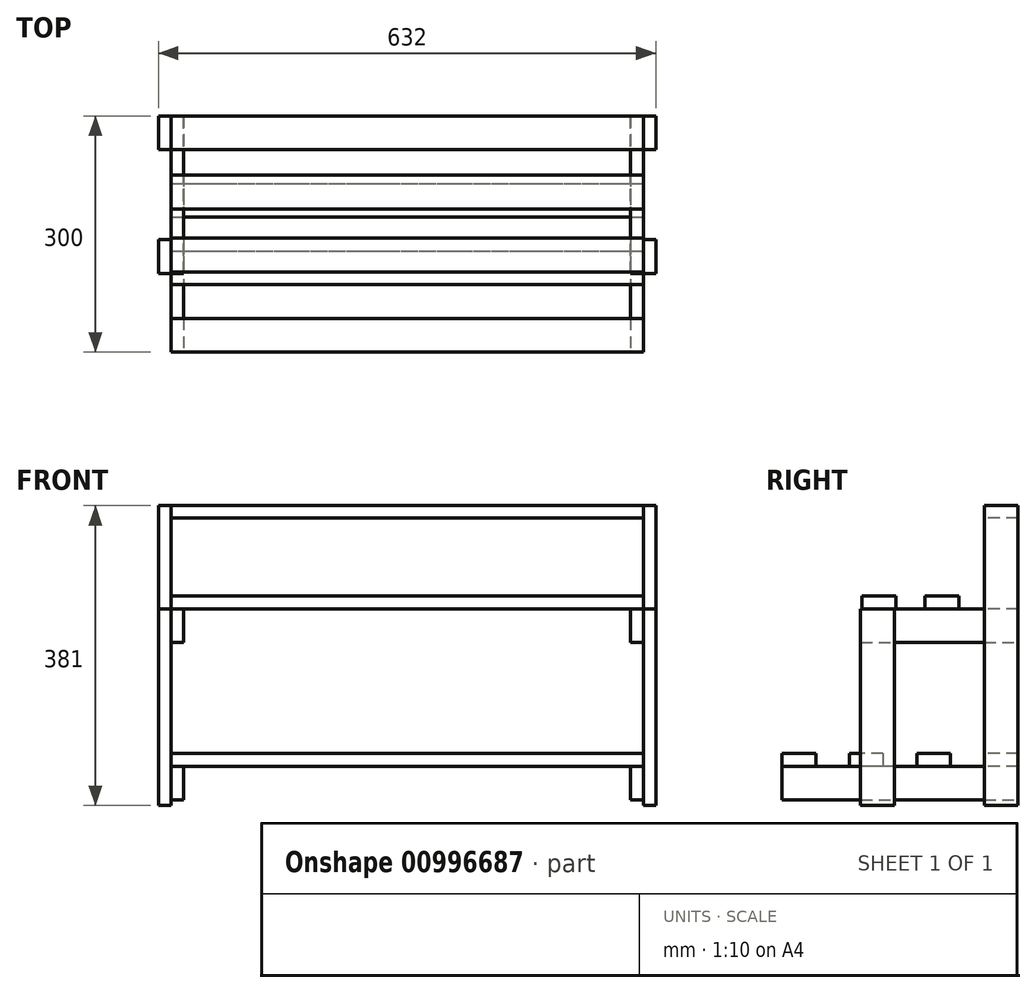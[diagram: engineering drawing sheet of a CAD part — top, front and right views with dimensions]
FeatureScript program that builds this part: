
annotation { "Feature Type Name" : "Feature", "Feature Type Description" : "" }
export const myFeature = defineFeature(function(context is Context, id is Id, definition is map)
    precondition{}
    {
        {
            var Q0;
            Q0=qCreatedBy(makeId("Top.planeOp"),FACE);
            var sketch = newSketch(context, id + "F0", { "sketchPlane" : qUnion([Q0])});
            skLineSegment(sketch, "E0.bottom", {"start": v(-351.68, 45.9) * mm, "end": v(248.32, 45.9) * mm});
            skLineSegment(sketch, "E0.top", {"start": v(-351.68, 2.9) * mm, "end": v(248.32, 2.9) * mm});
            skLineSegment(sketch, "E0.left", {"start": v(-351.68, 45.9) * mm, "end": v(-351.68, 2.9) * mm});
            skLineSegment(sketch, "E0.right", {"start": v(248.32, 45.9) * mm, "end": v(248.32, 2.9) * mm});
            skSolve(sketch);
        }
        {
            var Q0;
            Q0 = qSketchRegion(id + "F0", true);
            extrude(context, id + "F1", {"entities" : qUnion([Q0]), "depth" : 16 * mm, "offsetDistance" : 25 * mm});
        }
        {
            var Q0;
            Q0=makeQuery(id+"F1.opExtrude","SWEPT_BODY",BODY,{"disambiguationData":[OSD([sQuery(id+"F0.wireOp",EDGE,"E0.bottom"),sQuery(id+"F0.wireOp",EDGE,"E0.top"),sQuery(id+"F0.wireOp",EDGE,"E0.left"),sQuery(id+"F0.wireOp",EDGE,"E0.right")])]});
            transform(context, id + "F2", {"entities" : qUnion([Q0]), "transformType" : TransformType.TRANSLATION_3D, "dx" : 0 * mm, "dy" : -50 * mm, "dz" : -115 * mm, "makeCopy" : true});
        }
        {
            var Q0;
            Q0=makeQuery(id+"F2.opPattern","COPY",BODY,{"derivedFrom":makeQuery(id+"F1.opExtrude","SWEPT_BODY",BODY,{"disambiguationData":[OSD([sQuery(id+"F0.wireOp",EDGE,"E0.bottom"),sQuery(id+"F0.wireOp",EDGE,"E0.top"),sQuery(id+"F0.wireOp",EDGE,"E0.left"),sQuery(id+"F0.wireOp",EDGE,"E0.right")])]}),"instanceName":"1"});
            transform(context, id + "F3", {"entities" : qUnion([Q0]), "transformType" : TransformType.TRANSLATION_3D, "dx" : 0 * mm, "dy" : -95 * mm, "dz" : 0 * mm, "makeCopy" : true});
        }
        {
            var Q0;
            Q0=makeQuery(id+"F3.opPattern","COPY",BODY,{"derivedFrom":makeQuery(id+"F2.opPattern","COPY",BODY,{"derivedFrom":makeQuery(id+"F1.opExtrude","SWEPT_BODY",BODY,{"disambiguationData":[OSD([sQuery(id+"F0.wireOp",EDGE,"E0.bottom"),sQuery(id+"F0.wireOp",EDGE,"E0.top"),sQuery(id+"F0.wireOp",EDGE,"E0.left"),sQuery(id+"F0.wireOp",EDGE,"E0.right")])]}),"instanceName":"1"}),"instanceName":"1"});
            transform(context, id + "F4", {"entities" : qUnion([Q0]), "transformType" : TransformType.TRANSLATION_3D, "dx" : 0 * mm, "dy" : -155 * mm, "dz" : -200 * mm, "makeCopy" : true});
        }
        {
            var Q0;
            Q0=makeQuery(id+"F4.opPattern","COPY",BODY,{"derivedFrom":makeQuery(id+"F3.opPattern","COPY",BODY,{"derivedFrom":makeQuery(id+"F2.opPattern","COPY",BODY,{"derivedFrom":makeQuery(id+"F1.opExtrude","SWEPT_BODY",BODY,{"disambiguationData":[OSD([sQuery(id+"F0.wireOp",EDGE,"E0.bottom"),sQuery(id+"F0.wireOp",EDGE,"E0.top"),sQuery(id+"F0.wireOp",EDGE,"E0.left"),sQuery(id+"F0.wireOp",EDGE,"E0.right")])]}),"instanceName":"1"}),"instanceName":"1"}),"instanceName":"1"});
            transform(context, id + "F5", {"entities" : qUnion([Q0]), "transformType" : TransformType.TRANSLATION_3D, "dx" : 0 * mm, "dy" : 100 * mm, "dz" : 0 * mm, "makeCopy" : true});
        }
        {
            var Q0;
            Q0=makeQuery(id+"F5.opPattern","COPY",BODY,{"derivedFrom":makeQuery(id+"F4.opPattern","COPY",BODY,{"derivedFrom":makeQuery(id+"F3.opPattern","COPY",BODY,{"derivedFrom":makeQuery(id+"F2.opPattern","COPY",BODY,{"derivedFrom":makeQuery(id+"F1.opExtrude","SWEPT_BODY",BODY,{"disambiguationData":[OSD([sQuery(id+"F0.wireOp",EDGE,"E0.bottom"),sQuery(id+"F0.wireOp",EDGE,"E0.top"),sQuery(id+"F0.wireOp",EDGE,"E0.left"),sQuery(id+"F0.wireOp",EDGE,"E0.right")])]}),"instanceName":"1"}),"instanceName":"1"}),"instanceName":"1"}),"instanceName":"1"});
            transform(context, id + "F6", {"entities" : qUnion([Q0]), "transformType" : TransformType.TRANSLATION_3D, "dx" : 0 * mm, "dy" : 100 * mm, "dz" : 0 * mm, "makeCopy" : true});
        }
        {
            var Q0;
            Q0=makeQuery(id+"F6.opPattern","COPY",BODY,{"derivedFrom":makeQuery(id+"F5.opPattern","COPY",BODY,{"derivedFrom":makeQuery(id+"F4.opPattern","COPY",BODY,{"derivedFrom":makeQuery(id+"F3.opPattern","COPY",BODY,{"derivedFrom":makeQuery(id+"F2.opPattern","COPY",BODY,{"derivedFrom":makeQuery(id+"F1.opExtrude","SWEPT_BODY",BODY,{"disambiguationData":[OSD([sQuery(id+"F0.wireOp",EDGE,"E0.bottom"),sQuery(id+"F0.wireOp",EDGE,"E0.top"),sQuery(id+"F0.wireOp",EDGE,"E0.left"),sQuery(id+"F0.wireOp",EDGE,"E0.right")])]}),"instanceName":"1"}),"instanceName":"1"}),"instanceName":"1"}),"instanceName":"1"}),"instanceName":"1"});
            transform(context, id + "F7", {"entities" : qUnion([Q0]), "transformType" : TransformType.TRANSLATION_3D, "dx" : 0 * mm, "dy" : 100 * mm, "dz" : 0 * mm, "makeCopy" : true});
        }
        {
            var Q0;
            Q0=makeQuery(id+"F7.opPattern","COPY",FACE,{"derivedFrom":makeQuery(id+"F6.opPattern","COPY",FACE,{"derivedFrom":makeQuery(id+"F5.opPattern","COPY",FACE,{"derivedFrom":makeQuery(id+"F4.opPattern","COPY",FACE,{"derivedFrom":makeQuery(id+"F3.opPattern","COPY",FACE,{"derivedFrom":makeQuery(id+"F2.opPattern","COPY",FACE,{"derivedFrom":makeQuery(id+"F1.opExtrude","CAP_FACE",FACE,{"disambiguationData":[OSD([sQuery(id+"F0.wireOp",EDGE,"E0.bottom"),sQuery(id+"F0.wireOp",EDGE,"E0.top"),sQuery(id+"F0.wireOp",EDGE,"E0.left"),sQuery(id+"F0.wireOp",EDGE,"E0.right")])],"isStart":true}),"instanceName":"1"}),"instanceName":"1"}),"instanceName":"1"}),"instanceName":"1"}),"instanceName":"1"}),"instanceName":"1"});
            var sketch = newSketch(context, id + "F8", { "sketchPlane" : qUnion([Q0])});
            skLineSegment(sketch, "E1.bottom", {"start": v(-351.68, -45.9) * mm, "end": v(-351.68, -45.9) * mm});
            skLineSegment(sketch, "E1.top", {"start": v(-351.68, -2.9) * mm, "end": v(-351.68, -2.9) * mm});
            skLineSegment(sketch, "E1.left", {"start": v(-351.68, -45.9) * mm, "end": v(-351.68, -2.9) * mm});
            skLineSegment(sketch, "E1.right", {"start": v(-351.68, -45.9) * mm, "end": v(-351.68, -2.9) * mm});
            skLineSegment(sketch, "E2.bottom", {"start": v(-367.68, -2.9) * mm, "end": v(-351.68, -2.9) * mm});
            skLineSegment(sketch, "E2.top", {"start": v(-367.68, -45.9) * mm, "end": v(-351.68, -45.9) * mm});
            skLineSegment(sketch, "E2.left", {"start": v(-367.68, -2.9) * mm, "end": v(-367.68, -45.9) * mm});
            skLineSegment(sketch, "E2.right", {"start": v(-351.68, -2.9) * mm, "end": v(-351.68, -45.9) * mm});
            skSolve(sketch);
        }
        {
            var Q0;
            Q0=makeQuery(id+"F8.imprint","IMPRINT",FACE,{"disambiguationData":[TD([[makeQuery(id+"F8.imprint","IMPRINT",EDGE,{"derivedFrom":sQuery(id+"F8.wireOp",EDGE,"E2.bottom")}),-1.0]])]});
            var Q1;
            Q1=makeQuery(id+"F1.opExtrude","CAP_FACE",FACE,{"disambiguationData":[OSD([sQuery(id+"F0.wireOp",EDGE,"E0.bottom"),sQuery(id+"F0.wireOp",EDGE,"E0.top"),sQuery(id+"F0.wireOp",EDGE,"E0.left"),sQuery(id+"F0.wireOp",EDGE,"E0.right")])],"isStart":false});
            extrude(context, id + "F9", {"entities" : qUnion([Q0]), "endBound" : BoundingType.UP_TO_SURFACE, "oppositeDirection" : true, "depth" : 25 * mm, "endBoundEntityFace" : qUnion([Q1]), "offsetDistance" : 25 * mm, "hasSecondDirection" : true, "secondDirectionOppositeDirection" : false, "secondDirectionDepth" : 50 * mm});
        }
        {
            var Q0;
            Q0=makeQuery(id+"F9.opExtrude","SWEPT_BODY",BODY,{"disambiguationData":[OSD([sQuery(id+"F8.wireOp",EDGE,"E2.bottom"),sQuery(id+"F8.wireOp",EDGE,"E2.top"),sQuery(id+"F8.wireOp",EDGE,"E2.left"),sQuery(id+"F8.wireOp",EDGE,"E2.right")])]});
            var Q1;
            Q1=makeQuery(id+"F7.opPattern","COPY",EDGE,{"derivedFrom":makeQuery(id+"F6.opPattern","COPY",EDGE,{"derivedFrom":makeQuery(id+"F5.opPattern","COPY",EDGE,{"derivedFrom":makeQuery(id+"F4.opPattern","COPY",EDGE,{"derivedFrom":makeQuery(id+"F3.opPattern","COPY",EDGE,{"derivedFrom":makeQuery(id+"F2.opPattern","COPY",EDGE,{"derivedFrom":makeQuery(id+"F1.opExtrude","CAP_EDGE",EDGE,{"disambiguationData":[OSD([sQuery(id+"F0.wireOp",EDGE,"E0.bottom")])],"isStart":true}),"instanceName":"1"}),"instanceName":"1"}),"instanceName":"1"}),"instanceName":"1"}),"instanceName":"1"}),"instanceName":"1"});
            var Q2;
            Q2=makeQuery(id+"F7.opPattern","COPY",EDGE,{"derivedFrom":makeQuery(id+"F6.opPattern","COPY",EDGE,{"derivedFrom":makeQuery(id+"F5.opPattern","COPY",EDGE,{"derivedFrom":makeQuery(id+"F4.opPattern","COPY",EDGE,{"derivedFrom":makeQuery(id+"F3.opPattern","COPY",EDGE,{"derivedFrom":makeQuery(id+"F2.opPattern","COPY",EDGE,{"derivedFrom":makeQuery(id+"F1.opExtrude","CAP_EDGE",EDGE,{"disambiguationData":[OSD([sQuery(id+"F0.wireOp",EDGE,"E0.bottom")])],"isStart":true}),"instanceName":"1"}),"instanceName":"1"}),"instanceName":"1"}),"instanceName":"1"}),"instanceName":"1"}),"instanceName":"1"});
            transform(context, id + "F10", {"entities" : qUnion([Q0]), "transformType" : TransformType.TRANSLATION_DISTANCE, "transformDirection" : qUnion([Q2]), "distance" : 616 * mm, "makeCopy" : true});
        }
        {
            var Q0;
            Q0=makeQuery(id+"F2.opPattern","COPY",FACE,{"derivedFrom":makeQuery(id+"F1.opExtrude","SWEPT_FACE",FACE,{"disambiguationData":[OSD([sQuery(id+"F0.wireOp",EDGE,"E0.left")])]}),"instanceName":"1"});
            var sketch = newSketch(context, id + "F11", { "sketchPlane" : qUnion([Q0])});
            skLineSegment(sketch, "E3", {"start": v(-45.9, -115) * mm, "end": v(202.8, -115) * mm});
            skLineSegment(sketch, "E4", {"start": v(202.8, -115) * mm, "end": v(202.8, -158) * mm});
            skLineSegment(sketch, "E5", {"start": v(202.8, -158) * mm, "end": v(-45.9, -158) * mm});
            skLineSegment(sketch, "E6", {"start": v(-45.9, -158) * mm, "end": v(-45.9, -115) * mm});
            skSolve(sketch);
        }
        {
            var Q0;
            Q0 = qSketchRegion(id + "F11", true);
            extrude(context, id + "F12", {"entities" : qUnion([Q0]), "oppositeDirection" : true, "depth" : 16 * mm, "offsetDistance" : 25 * mm});
        }
        {
            var Q0;
            Q0=makeQuery(id+"F12.opExtrude","SWEPT_BODY",BODY,{"disambiguationData":[OSD([sQuery(id+"F11.wireOp",EDGE,"E3"),sQuery(id+"F11.wireOp",EDGE,"E4"),sQuery(id+"F11.wireOp",EDGE,"E5"),sQuery(id+"F11.wireOp",EDGE,"E6")])]});
            var Q1;
            Q1=makeQuery(id+"F2.opPattern","COPY",EDGE,{"derivedFrom":makeQuery(id+"F1.opExtrude","CAP_EDGE",EDGE,{"disambiguationData":[OSD([sQuery(id+"F0.wireOp",EDGE,"E0.bottom")])],"isStart":true}),"instanceName":"1"});
            transform(context, id + "F13", {"entities" : qUnion([Q0]), "transformType" : TransformType.TRANSLATION_DISTANCE, "transformDirection" : qUnion([Q1]), "distance" : (600 - 16) * mm, "makeCopy" : true});
        }
        {
            var Q0;
            Q0=makeQuery(id+"F2.opPattern","COPY",BODY,{"derivedFrom":makeQuery(id+"F1.opExtrude","SWEPT_BODY",BODY,{"disambiguationData":[OSD([sQuery(id+"F0.wireOp",EDGE,"E0.bottom"),sQuery(id+"F0.wireOp",EDGE,"E0.top"),sQuery(id+"F0.wireOp",EDGE,"E0.left"),sQuery(id+"F0.wireOp",EDGE,"E0.right")])]}),"instanceName":"1"});
            var Q1;
            Q1=makeQuery(id+"F12.opExtrude","CAP_EDGE",EDGE,{"disambiguationData":[OSD([sQuery(id+"F11.wireOp",EDGE,"E3")])],"isStart":false});
            transform(context, id + "F14", {"entities" : qUnion([Q0]), "transformType" : TransformType.TRANSLATION_DISTANCE, "transformDirection" : qUnion([Q1]), "distance" : 25 * mm, "makeCopy" : false});
        }
        {
            var Q0;
            Q0=makeQuery(id+"F3.opPattern","COPY",BODY,{"derivedFrom":makeQuery(id+"F2.opPattern","COPY",BODY,{"derivedFrom":makeQuery(id+"F1.opExtrude","SWEPT_BODY",BODY,{"disambiguationData":[OSD([sQuery(id+"F0.wireOp",EDGE,"E0.bottom"),sQuery(id+"F0.wireOp",EDGE,"E0.top"),sQuery(id+"F0.wireOp",EDGE,"E0.left"),sQuery(id+"F0.wireOp",EDGE,"E0.right")])]}),"instanceName":"1"}),"instanceName":"1"});
            var Q1;
            Q1=makeQuery(id+"F12.opExtrude","CAP_EDGE",EDGE,{"disambiguationData":[OSD([sQuery(id+"F11.wireOp",EDGE,"E3")])],"isStart":false});
            transform(context, id + "F15", {"entities" : qUnion([Q0]), "transformType" : TransformType.TRANSLATION_DISTANCE, "transformDirection" : qUnion([Q1]), "distance" : 25 * mm, "makeCopy" : false});
        }
        {
            var Q0;
            Q0=makeQuery(id+"F12.opExtrude","SWEPT_BODY",BODY,{"disambiguationData":[OSD([sQuery(id+"F11.wireOp",EDGE,"E3"),sQuery(id+"F11.wireOp",EDGE,"E4"),sQuery(id+"F11.wireOp",EDGE,"E5"),sQuery(id+"F11.wireOp",EDGE,"E6")])]});
            var Q1;
            Q1=makeQuery(id+"F9.opExtrude","SWEPT_EDGE",EDGE,{"disambiguationData":[OSD([sQuery(id+"F0.wireOp",EDGE,"E0.bottom"),sQuery(id+"F8.wireOp",EDGE,"E2.top"),sQuery(id+"F8.wireOp",EDGE,"E2.right")])]});
            transform(context, id + "F16", {"entities" : qUnion([Q0]), "transformType" : TransformType.TRANSLATION_DISTANCE, "transformDirection" : qUnion([Q1]), "distance" : 200 * mm, "makeCopy" : true});
        }
        {
            var Q0;
            Q0=makeQuery(id+"F16.opPattern","COPY",FACE,{"derivedFrom":makeQuery(id+"F12.opExtrude","SWEPT_FACE",FACE,{"disambiguationData":[OSD([sQuery(id+"F11.wireOp",EDGE,"E4")])]}),"instanceName":"1"});
            extrude(context, id + "F17", {"entities" : qUnion([Q0]), "operationType" : NewBodyOperationType.ADD, "depth" : 51.3 * mm, "offsetDistance" : 25 * mm});
        }
        {
            var Q0;
            Q0=makeQuery(id+"F12.opExtrude","SWEPT_FACE",FACE,{"disambiguationData":[OSD([sQuery(id+"F11.wireOp",EDGE,"E4")])]});
            extrude(context, id + "F18", {"entities" : qUnion([Q0]), "operationType" : NewBodyOperationType.REMOVE, "oppositeDirection" : true, "depth" : 48.7 * mm, "offsetDistance" : 25 * mm});
        }
        {
            var Q0;
            Q0=makeQuery(id+"F13.opPattern","COPY",FACE,{"derivedFrom":makeQuery(id+"F12.opExtrude","SWEPT_FACE",FACE,{"disambiguationData":[OSD([sQuery(id+"F11.wireOp",EDGE,"E4")])]}),"instanceName":"1"});
            extrude(context, id + "F19", {"entities" : qUnion([Q0]), "operationType" : NewBodyOperationType.REMOVE, "oppositeDirection" : true, "depth" : 48.7 * mm, "offsetDistance" : 25 * mm});
        }
        {
            var Q0;
            Q0=makeQuery(id+"F3.opPattern","COPY",BODY,{"derivedFrom":makeQuery(id+"F2.opPattern","COPY",BODY,{"derivedFrom":makeQuery(id+"F1.opExtrude","SWEPT_BODY",BODY,{"disambiguationData":[OSD([sQuery(id+"F0.wireOp",EDGE,"E0.bottom"),sQuery(id+"F0.wireOp",EDGE,"E0.top"),sQuery(id+"F0.wireOp",EDGE,"E0.left"),sQuery(id+"F0.wireOp",EDGE,"E0.right")])]}),"instanceName":"1"}),"instanceName":"1"});
            deleteBodies(context, id + "F20", {"entities" : qUnion([Q0])});
        }
        {
            var Q0;
            Q0=makeQuery(id+"F2.opPattern","COPY",BODY,{"derivedFrom":makeQuery(id+"F1.opExtrude","SWEPT_BODY",BODY,{"disambiguationData":[OSD([sQuery(id+"F0.wireOp",EDGE,"E0.bottom"),sQuery(id+"F0.wireOp",EDGE,"E0.top"),sQuery(id+"F0.wireOp",EDGE,"E0.left"),sQuery(id+"F0.wireOp",EDGE,"E0.right")])]}),"instanceName":"1"});
            transform(context, id + "F21", {"entities" : qUnion([Q0]), "transformType" : TransformType.TRANSLATION_3D, "dx" : 0 * mm, "dy" : -80 * mm, "dz" : 0 * mm, "makeCopy" : true});
        }
        {
            var Q0;
            Q0=makeQuery(id+"F16.opPattern","COPY",BODY,{"derivedFrom":makeQuery(id+"F12.opExtrude","SWEPT_BODY",BODY,{"disambiguationData":[OSD([sQuery(id+"F11.wireOp",EDGE,"E3"),sQuery(id+"F11.wireOp",EDGE,"E4"),sQuery(id+"F11.wireOp",EDGE,"E5"),sQuery(id+"F11.wireOp",EDGE,"E6")])]}),"instanceName":"1"});
            transform(context, id + "F22", {"entities" : qUnion([Q0]), "transformType" : TransformType.TRANSLATION_3D, "dx" : (600 - 16) * mm, "dy" : 0 * mm, "dz" : 0 * mm, "makeCopy" : true});
        }
        {
            var Q0;
            Q0=makeQuery(id+"F12.opExtrude","CAP_FACE",FACE,{"disambiguationData":[OSD([sQuery(id+"F11.wireOp",EDGE,"E3"),sQuery(id+"F11.wireOp",EDGE,"E4"),sQuery(id+"F11.wireOp",EDGE,"E5"),sQuery(id+"F11.wireOp",EDGE,"E6")])],"isStart":true});
            var sketch = newSketch(context, id + "F23", { "sketchPlane" : qUnion([Q0])});
            skLineSegment(sketch, "E7", {"start": v(154.1, -158) * mm, "end": v(154.1, -115) * mm});
            skLineSegment(sketch, "E8", {"start": v(154.1, -115) * mm, "end": v(111.1, -115) * mm});
            skLineSegment(sketch, "E9", {"start": v(111.1, -115) * mm, "end": v(111.1, -365) * mm});
            skLineSegment(sketch, "E10", {"start": v(111.1, -365) * mm, "end": v(154.1, -365) * mm});
            skLineSegment(sketch, "E11", {"start": v(154.1, -365) * mm, "end": v(154.1, -158) * mm});
            skSolve(sketch);
        }
        {
            var Q0;
            {var subQ0=sQuery(id+"F23.wireOp",EDGE,"E10");Q0=makeQuery(id+"F23.imprint","IMPRINT",FACE,{"disambiguationData":[TD([[makeQuery(id+"F23.imprint","IMPRINT",EDGE,{"derivedFrom":subQ0}),1.0]])]});}
            var Q1;
            {var subQ0=sQuery(id+"F23.wireOp",EDGE,"E7");Q1=makeQuery(id+"F23.imprint","IMPRINT",FACE,{"disambiguationData":[TD([[makeQuery(id+"F23.imprint","IMPRINT",EDGE,{"derivedFrom":subQ0}),-1.0]])]});}
            extrude(context, id + "F24", {"entities" : qUnion([Q0, Q1]), "depth" : 16 * mm, "offsetDistance" : 25 * mm});
        }
        {
            var Q0;
            Q0=makeQuery(id+"F4.opPattern","COPY",BODY,{"derivedFrom":makeQuery(id+"F3.opPattern","COPY",BODY,{"derivedFrom":makeQuery(id+"F2.opPattern","COPY",BODY,{"derivedFrom":makeQuery(id+"F1.opExtrude","SWEPT_BODY",BODY,{"disambiguationData":[OSD([sQuery(id+"F0.wireOp",EDGE,"E0.bottom"),sQuery(id+"F0.wireOp",EDGE,"E0.top"),sQuery(id+"F0.wireOp",EDGE,"E0.left"),sQuery(id+"F0.wireOp",EDGE,"E0.right")])]}),"instanceName":"1"}),"instanceName":"1"}),"instanceName":"1"});
            var Q1;
            {var subQ0=sQuery(id+"F11.wireOp",EDGE,"E4");var subQ1=sQuery(id+"F11.wireOp",EDGE,"E3");Q1=makeQuery(id+"F17.boolean.opBoolean","MERGE",EDGE,{"derivedFrom":[makeQuery(id+"F16.opPattern","COPY",EDGE,{"derivedFrom":makeQuery(id+"F12.opExtrude","CAP_EDGE",EDGE,{"disambiguationData":[OSD([subQ1])],"isStart":true}),"instanceName":"1"}),makeQuery(id+"F17.opExtrude","SWEPT_EDGE",EDGE,{"disambiguationData":[OSD([subQ1,subQ0]),TDD([makeQuery(id+"F16.opPattern","COPY",VERTEX,{"derivedFrom":makeQuery(id+"F12.opExtrude","CAP_VERTEX",VERTEX,{"disambiguationData":[OSD([subQ1,subQ0])],"isStart":true}),"instanceName":"1"})])]})]});}
            transform(context, id + "F25", {"entities" : qUnion([Q0]), "transformType" : TransformType.TRANSLATION_DISTANCE, "transformDirection" : qUnion([Q1]), "distance" : 43 * mm, "oppositeDirection" : true, "makeCopy" : false});
        }
        {
            var Q0;
            Q0=makeQuery(id+"F5.opPattern","COPY",BODY,{"derivedFrom":makeQuery(id+"F4.opPattern","COPY",BODY,{"derivedFrom":makeQuery(id+"F3.opPattern","COPY",BODY,{"derivedFrom":makeQuery(id+"F2.opPattern","COPY",BODY,{"derivedFrom":makeQuery(id+"F1.opExtrude","SWEPT_BODY",BODY,{"disambiguationData":[OSD([sQuery(id+"F0.wireOp",EDGE,"E0.bottom"),sQuery(id+"F0.wireOp",EDGE,"E0.top"),sQuery(id+"F0.wireOp",EDGE,"E0.left"),sQuery(id+"F0.wireOp",EDGE,"E0.right")])]}),"instanceName":"1"}),"instanceName":"1"}),"instanceName":"1"}),"instanceName":"1"});
            deleteBodies(context, id + "F26", {"entities" : qUnion([Q0])});
        }
        {
            var Q0;
            Q0=makeQuery(id+"F6.opPattern","COPY",BODY,{"derivedFrom":makeQuery(id+"F5.opPattern","COPY",BODY,{"derivedFrom":makeQuery(id+"F4.opPattern","COPY",BODY,{"derivedFrom":makeQuery(id+"F3.opPattern","COPY",BODY,{"derivedFrom":makeQuery(id+"F2.opPattern","COPY",BODY,{"derivedFrom":makeQuery(id+"F1.opExtrude","SWEPT_BODY",BODY,{"disambiguationData":[OSD([sQuery(id+"F0.wireOp",EDGE,"E0.bottom"),sQuery(id+"F0.wireOp",EDGE,"E0.top"),sQuery(id+"F0.wireOp",EDGE,"E0.left"),sQuery(id+"F0.wireOp",EDGE,"E0.right")])]}),"instanceName":"1"}),"instanceName":"1"}),"instanceName":"1"}),"instanceName":"1"}),"instanceName":"1"});
            deleteBodies(context, id + "F27", {"entities" : qUnion([Q0])});
        }
        {
            var Q0;
            Q0=makeQuery(id+"F4.opPattern","COPY",BODY,{"derivedFrom":makeQuery(id+"F3.opPattern","COPY",BODY,{"derivedFrom":makeQuery(id+"F2.opPattern","COPY",BODY,{"derivedFrom":makeQuery(id+"F1.opExtrude","SWEPT_BODY",BODY,{"disambiguationData":[OSD([sQuery(id+"F0.wireOp",EDGE,"E0.bottom"),sQuery(id+"F0.wireOp",EDGE,"E0.top"),sQuery(id+"F0.wireOp",EDGE,"E0.left"),sQuery(id+"F0.wireOp",EDGE,"E0.right")])]}),"instanceName":"1"}),"instanceName":"1"}),"instanceName":"1"});
            var Q1;
            {var subQ0=sQuery(id+"F11.wireOp",EDGE,"E4");var subQ1=sQuery(id+"F11.wireOp",EDGE,"E3");Q1=makeQuery(id+"F17.boolean.opBoolean","MERGE",EDGE,{"derivedFrom":[makeQuery(id+"F16.opPattern","COPY",EDGE,{"derivedFrom":makeQuery(id+"F12.opExtrude","CAP_EDGE",EDGE,{"disambiguationData":[OSD([subQ1])],"isStart":true}),"instanceName":"1"}),makeQuery(id+"F17.opExtrude","SWEPT_EDGE",EDGE,{"disambiguationData":[OSD([subQ1,subQ0]),TDD([makeQuery(id+"F16.opPattern","COPY",VERTEX,{"derivedFrom":makeQuery(id+"F12.opExtrude","CAP_VERTEX",VERTEX,{"disambiguationData":[OSD([subQ1,subQ0])],"isStart":true}),"instanceName":"1"})])]})]});}
            transform(context, id + "F28", {"entities" : qUnion([Q0]), "transformType" : TransformType.TRANSLATION_DISTANCE, "transformDirection" : qUnion([Q1]), "distance" : 85.67 * mm, "oppositeDirection" : true, "makeCopy" : true});
        }
        {
            var Q0;
            Q0=makeQuery(id+"F4.opPattern","COPY",BODY,{"derivedFrom":makeQuery(id+"F3.opPattern","COPY",BODY,{"derivedFrom":makeQuery(id+"F2.opPattern","COPY",BODY,{"derivedFrom":makeQuery(id+"F1.opExtrude","SWEPT_BODY",BODY,{"disambiguationData":[OSD([sQuery(id+"F0.wireOp",EDGE,"E0.bottom"),sQuery(id+"F0.wireOp",EDGE,"E0.top"),sQuery(id+"F0.wireOp",EDGE,"E0.left"),sQuery(id+"F0.wireOp",EDGE,"E0.right")])]}),"instanceName":"1"}),"instanceName":"1"}),"instanceName":"1"});
            var Q1;
            {var subQ0=sQuery(id+"F11.wireOp",EDGE,"E4");var subQ1=sQuery(id+"F11.wireOp",EDGE,"E3");Q1=makeQuery(id+"F17.boolean.opBoolean","MERGE",EDGE,{"derivedFrom":[makeQuery(id+"F16.opPattern","COPY",EDGE,{"derivedFrom":makeQuery(id+"F12.opExtrude","CAP_EDGE",EDGE,{"disambiguationData":[OSD([subQ1])],"isStart":true}),"instanceName":"1"}),makeQuery(id+"F17.opExtrude","SWEPT_EDGE",EDGE,{"disambiguationData":[OSD([subQ1,subQ0]),TDD([makeQuery(id+"F16.opPattern","COPY",VERTEX,{"derivedFrom":makeQuery(id+"F12.opExtrude","CAP_VERTEX",VERTEX,{"disambiguationData":[OSD([subQ1,subQ0])],"isStart":true}),"instanceName":"1"})])]})]});}
            transform(context, id + "F29", {"entities" : qUnion([Q0]), "transformType" : TransformType.TRANSLATION_DISTANCE, "transformDirection" : qUnion([Q1]), "distance" : 171.33 * mm, "oppositeDirection" : true, "makeCopy" : true});
        }
        {
            var Q0;
            Q0=makeQuery(id+"F24.opExtrude","SWEPT_BODY",BODY,{"disambiguationData":[OSD([sQuery(id+"F23.wireOp",EDGE,"E7"),sQuery(id+"F23.wireOp",EDGE,"E8"),sQuery(id+"F23.wireOp",EDGE,"E9"),sQuery(id+"F23.wireOp",EDGE,"E10"),sQuery(id+"F23.wireOp",EDGE,"E11")])]});
            var Q1;
            Q1=makeQuery(id+"F4.opPattern","COPY",EDGE,{"derivedFrom":makeQuery(id+"F3.opPattern","COPY",EDGE,{"derivedFrom":makeQuery(id+"F2.opPattern","COPY",EDGE,{"derivedFrom":makeQuery(id+"F1.opExtrude","CAP_EDGE",EDGE,{"disambiguationData":[OSD([sQuery(id+"F0.wireOp",EDGE,"E0.top")])],"isStart":false}),"instanceName":"1"}),"instanceName":"1"}),"instanceName":"1"});
            transform(context, id + "F30", {"entities" : qUnion([Q0]), "transformType" : TransformType.TRANSLATION_DISTANCE, "transformDirection" : qUnion([Q1]), "distance" : (600 + 16) * mm, "makeCopy" : true});
        }
    });
